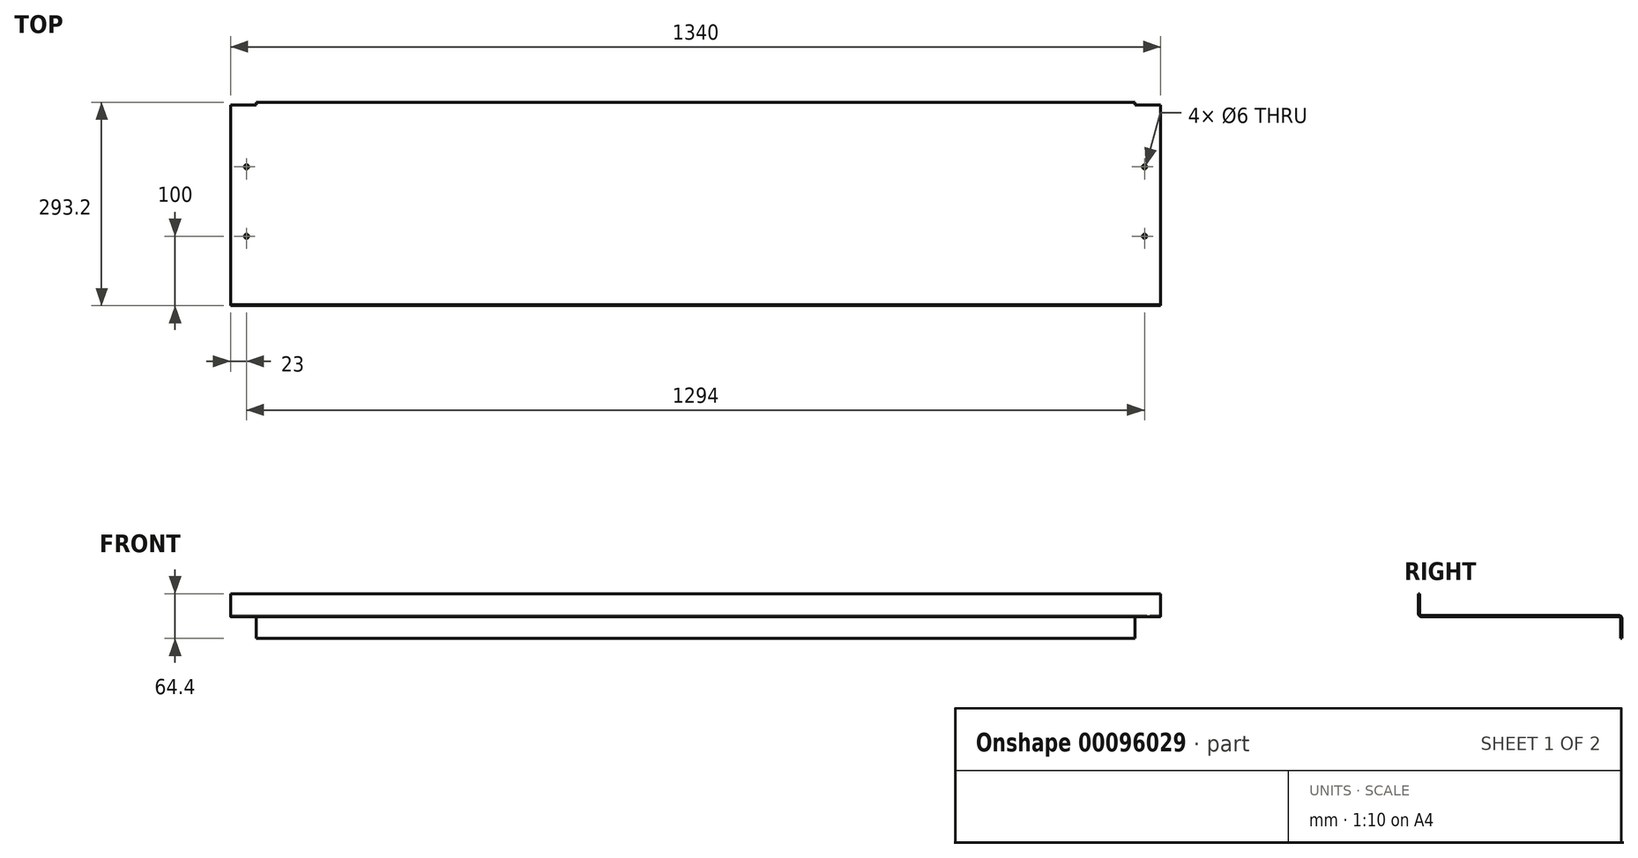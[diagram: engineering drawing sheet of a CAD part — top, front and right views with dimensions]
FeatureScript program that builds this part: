
annotation { "Feature Type Name" : "Feature", "Feature Type Description" : "" }
export const myFeature = defineFeature(function(context is Context, id is Id, definition is map)
    precondition{}
    {
        {
            var Q0;
            Q0=qCreatedBy(makeId("Right.planeOp"),FACE);
            var sketch = newSketch(context, id + "F0", { "sketchPlane" : qUnion([Q0])});
            skLineSegment(sketch, "E0", {"start": v(145, 0) * mm, "end": v(-146.6, 0) * mm});
            skLineSegment(sketch, "E1", {"start": v(-146.6, 0) * mm, "end": v(-146.6, 33) * mm});
            skLineSegment(sketch, "E2", {"start": v(145, 0) * mm, "end": v(145, -31.4) * mm});
            skLineSegment(sketch, "E3", {"start": v(-146.6, 33) * mm, "end": v(-145, 33) * mm});
            skLineSegment(sketch, "E4", {"start": v(-145, 33) * mm, "end": v(-145, 1.6) * mm});
            skLineSegment(sketch, "E5", {"start": v(-145, 1.6) * mm, "end": v(146.6, 1.6) * mm});
            skLineSegment(sketch, "E6", {"start": v(146.6, 1.6) * mm, "end": v(146.6, -31.4) * mm});
            skLineSegment(sketch, "E7", {"start": v(146.6, -31.4) * mm, "end": v(145, -31.4) * mm});
            skSolve(sketch);
        }
        {
            var Q0;
            Q0 = qSketchRegion(id + "F0", true);
            extrude(context, id + "F1", {"entities" : qUnion([Q0]), "endBound" : BoundingType.SYMMETRIC, "depth" : 1340 * mm});
        }
        {
            var Q0;
            Q0=makeQuery(id+"F1.opExtrude","SWEPT_EDGE",EDGE,{"disambiguationData":[OSD([sQuery(id+"F0.wireOp",EDGE,"E0"),sQuery(id+"F0.wireOp",EDGE,"E1")])]});
            var Q1;
            Q1=makeQuery(id+"F1.opExtrude","SWEPT_EDGE",EDGE,{"disambiguationData":[OSD([sQuery(id+"F0.wireOp",EDGE,"E5"),sQuery(id+"F0.wireOp",EDGE,"E6")])]});
            fillet(context, id + "F2", {"entities" : qUnion([Q0, Q1]), "radius" : 4 * mm, "tangentPropagation" : true, "allowEdgeOverflow" : false});
        }
        {
            var Q0;
            Q0=makeQuery(id+"F1.opExtrude","SWEPT_EDGE",EDGE,{"disambiguationData":[OSD([sQuery(id+"F0.wireOp",EDGE,"E4"),sQuery(id+"F0.wireOp",EDGE,"E5")])]});
            var Q1;
            Q1=makeQuery(id+"F1.opExtrude","SWEPT_EDGE",EDGE,{"disambiguationData":[OSD([sQuery(id+"F0.wireOp",EDGE,"E0"),sQuery(id+"F0.wireOp",EDGE,"E2")])]});
            fillet(context, id + "F3", {"entities" : qUnion([Q0, Q1]), "radius" : (4 - 1.6) * mm, "tangentPropagation" : true, "allowEdgeOverflow" : false});
        }
        {
            var Q0;
            Q0=makeQuery(id+"F1.opExtrude","SWEPT_FACE",FACE,{"disambiguationData":[OSD([sQuery(id+"F0.wireOp",EDGE,"E6")])]});
            var sketch = newSketch(context, id + "F4", { "sketchPlane" : qUnion([Q0])});
            skLineSegment(sketch, "E8.bottom", {"start": v(-670, -31.4) * mm, "end": v(-633, -31.4) * mm});
            skLineSegment(sketch, "E8.top", {"start": v(-670, 4) * mm, "end": v(-633, 4) * mm});
            skLineSegment(sketch, "E8.left", {"start": v(-670, -31.4) * mm, "end": v(-670, 4) * mm});
            skLineSegment(sketch, "E8.right", {"start": v(-633, -31.4) * mm, "end": v(-633, 4) * mm});
            skLineSegment(sketch, "E9.MirrorCS", {"start": v(670, -31.4) * mm, "end": v(670, 4) * mm});
            skLineSegment(sketch, "E10.MirrorCS", {"start": v(670, 4) * mm, "end": v(633, 4) * mm});
            skLineSegment(sketch, "E11.MirrorCS", {"start": v(633, -31.4) * mm, "end": v(633, 4) * mm});
            skLineSegment(sketch, "E12.MirrorCS", {"start": v(670, -31.4) * mm, "end": v(633, -31.4) * mm});
            skSolve(sketch);
        }
        {
            var Q0;
            Q0 = qSketchRegion(id + "F4", true);
            extrude(context, id + "F5", {"entities" : qUnion([Q0]), "operationType" : NewBodyOperationType.REMOVE, "oppositeDirection" : true, "depth" : 4 * mm});
        }
        {
            var Q0;
            Q0=makeQuery(id+"F1.opExtrude","SWEPT_FACE",FACE,{"disambiguationData":[OSD([sQuery(id+"F0.wireOp",EDGE,"E5")])]});
            var sketch = newSketch(context, id + "F6", { "sketchPlane" : qUnion([Q0])});
            skCircle(sketch, "E13", {"center": v(-647, -46.6) * mm, "radius": 3 * mm});
            skCircle(sketch, "E14", {"center": v(-647, 53.4) * mm, "radius": 3 * mm});
            skCircle(sketch, "E15.MirrorC", {"center": v(647, 53.4) * mm, "radius": 3 * mm});
            skCircle(sketch, "E16.MirrorC", {"center": v(647, -46.6) * mm, "radius": 3 * mm});
            skSolve(sketch);
        }
        {
            var Q0;
            Q0 = qSketchRegion(id + "F6", true);
            extrude(context, id + "F7", {"entities" : qUnion([Q0]), "operationType" : NewBodyOperationType.REMOVE, "oppositeDirection" : true, "depth" : 25 * mm});
        }
    });
